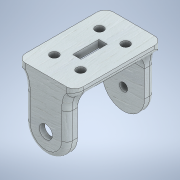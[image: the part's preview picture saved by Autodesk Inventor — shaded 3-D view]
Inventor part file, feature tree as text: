
AUTODESK INVENTOR PART (.ipt)
format: ipt  version: 2021 (Build 250183000, 183)  size: 526,336 bytes
history: native  units: mm
features: extrude x12, sketch x12, fillet x6, projected_geometry x5, plane x1, pattern_linear x1
ambient origin geometry x8: Origin, YZ Plane, XZ Plane, XY Plane, X Axis, Y Axis, Z Axis, Center Point
bodies: Solid1 (feature_tree)
feature tree (37):
  extrude  "Extrusion1"  Depth=40.0mm
  extrude  "Extrusion2"  Depth=5.0mm TaperAngle=0.0deg
  extrude  "Extrusion3"  Depth=5.0mm TaperAngle=0.0deg
  fillet  "Fillet1"  Radius=2.0mm
  plane  "Work Plane1"
  extrude  "Extrusion4"  Depth=64.0mm
  extrude  "Extrusion5"  Depth=7.0mm TaperAngle=0.0deg
  fillet  "Fillet2"  Radius=3.0mm
  extrude  "Extrusion6"  Depth=7.5mm
  pattern_linear  "Rectangular Pattern1"  Count1=2 Spacing1=71.0mm
  extrude  "Extrusion7"  Depth=5.0mm
  fillet  "Fillet3"  Radius=5.0mm
  fillet  "Fillet4"  Radius=15.0mm
  fillet  "Fillet5"  Radius=8.0mm
  extrude  "Extrusion8"  Depth=8.0mm
  extrude  "Extrusion9"  Depth=8.0mm
  extrude  "Extrusion10"  Depth=15.0mm
  extrude  "Extrusion11"  Depth=17.5mm
  extrude  "Extrusion12"  Depth=15.0mm
  fillet  "Fillet6"  Radius=17.5mm
  sketch  "Sketch1"  dims[d0=30.0mm d1=40.0mm]
  sketch  "Sketch2"  dims[d2=40.0mm d3=5.0mm d4=0.0mm]
  projected_geometry  "Projected Loop1"
  sketch  "Sketch3"  dims[d5=12.5mm d6=5.0mm d7=0.0mm d8=2.0mm d9=0.0mm]
  projected_geometry  "Projected Loop2"
  sketch  "Sketch4"  dims[d10=5.0mm d11=64.0mm]
  projected_geometry  "Projected Loop3"
  sketch  "Sketch5"  dims[d12=7.8mm d13=7.0mm d14=0.0mm d15=3.0mm d16=0.0mm]
  sketch  "Sketch6"  dims[d17=10.0mm d18=7.5mm]
  sketch  "Sketch7"  dims[d19=7.5mm]
  sketch  "Sketch8"  dims[d20=15.0mm]
  sketch  "Sketch9"  dims[d21=15.0mm]
  sketch  "Sketch11"  dims[d22=3.0mm d23=0.0mm d24=20.0mm d26=71.0mm]
  projected_geometry  "Projected Loop5"
  sketch  "Sketch12"  dims[d27=7.0mm d28=0.0mm d29=5.0mm d30=5.0mm d31=15.0mm d32=8.0mm]
  projected_geometry  "Projected Loop6"
  sketch  "Sketch14"  dims[d33=8.0mm d34=8.0mm d35=8.0mm d36=15.0mm d37=17.5mm d38=15.0mm d39=17.5mm d40=17.5mm d41=15.0mm d42=15.0mm d43=17.5mm d44=8.0mm d45=25.0mm d46=23.5mm d47=26.5mm d48=20.0mm d49=0.0mm d50=15.0mm d51=15.0mm d52=15.0mm d53=15.0mm d54=20.0mm d55=0.0mm d56=10.0mm d57=0.0mm d58=10.0mm d59=0.0mm d60=8.0mm d61=15.0mm d62=0.0mm d63=5.0mm]
